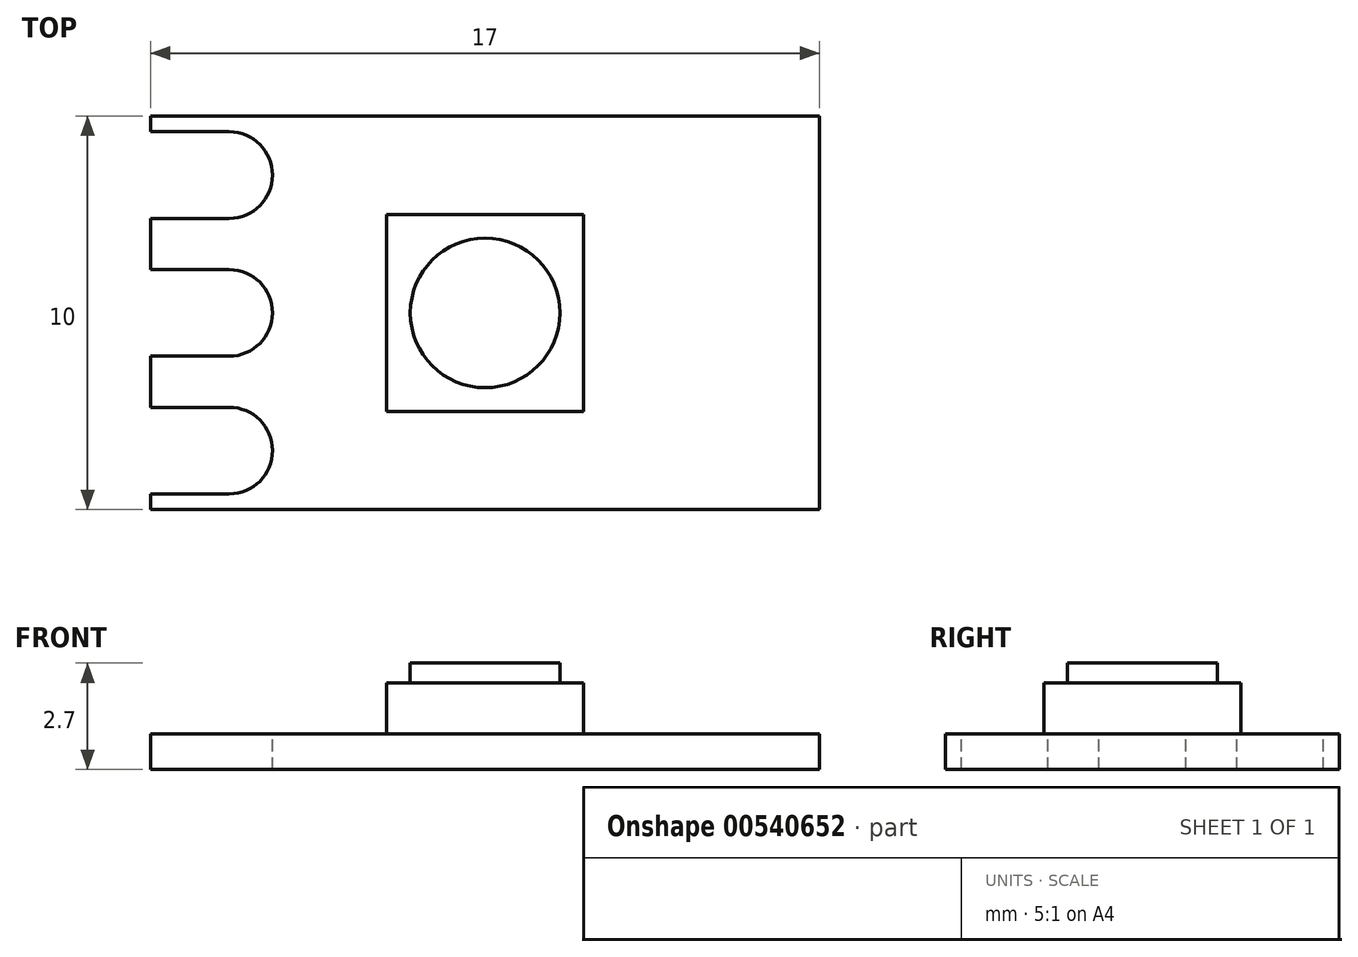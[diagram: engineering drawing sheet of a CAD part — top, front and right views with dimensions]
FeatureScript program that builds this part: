
annotation { "Feature Type Name" : "Feature", "Feature Type Description" : "" }
export const myFeature = defineFeature(function(context is Context, id is Id, definition is map)
    precondition{}
    {
        {
            var Q0;
            Q0=qCreatedBy(makeId("Top.planeOp"),FACE);
            var sketch = newSketch(context, id + "F0", { "sketchPlane" : qUnion([Q0])});
            skLineSegment(sketch, "E0.bottom", {"start": v(8.5, -5) * mm, "end": v(-8.5, -5) * mm});
            skLineSegment(sketch, "E0.top", {"start": v(8.5, 5) * mm, "end": v(-8.5, 5) * mm});
            skLineSegment(sketch, "E0.left", {"start": v(136, -5) * mm, "end": v(136, 5) * mm});
            skLineSegment(sketch, "E0.right", {"start": v(-8.5, -5) * mm, "end": v(-8.5, 5) * mm});
            skPoint(sketch, "E0.middle", {"position": v(0, 0) * mm});
            skLineSegment(sketch, "E1", {"start": v(8.5, 5) * mm, "end": v(8.5, -5) * mm});
            skLineSegment(sketch, "E2", {"start": v(-8.5, 0) * mm, "end": v(8.5, 0) * mm, "construction": true});
            skLineSegment(sketch, "E3.bottom", {"start": v(2.5, -2.5) * mm, "end": v(-2.5, -2.5) * mm});
            skLineSegment(sketch, "E3.top", {"start": v(2.5, 2.5) * mm, "end": v(-2.5, 2.5) * mm});
            skLineSegment(sketch, "E3.left", {"start": v(2.5, -2.5) * mm, "end": v(2.5, 2.5) * mm});
            skLineSegment(sketch, "E3.right", {"start": v(-2.5, -2.5) * mm, "end": v(-2.5, 2.5) * mm});
            skLineSegment(sketch, "E4", {"start": v(-8.5, 3.5) * mm, "end": v(-6.5, 3.5) * mm, "construction": true});
            skArc(sketch, "E5.0.endCap", {"start": v(-6.5, 4.6) * mm, "mid": v(-5.4, 3.5) * mm, "end": v(-6.5, 2.4) * mm});
            skLineSegment(sketch, "E5.0.left", {"start": v(-8.5, 4.6) * mm, "end": v(-6.5, 4.6) * mm});
            skLineSegment(sketch, "E5.0.right", {"start": v(-8.5, 2.4) * mm, "end": v(-6.5, 2.4) * mm});
            skLineSegment(sketch, "E6.0.1.0", {"start": v(-8.5, 0) * mm, "end": v(-6.5, 0) * mm, "construction": true});
            skArc(sketch, "E6.0.1.1", {"start": v(-6.5, 1.1) * mm, "mid": v(-5.4, 0) * mm, "end": v(-6.5, -1.1) * mm});
            skLineSegment(sketch, "E6.0.1.2", {"start": v(-8.5, 1.1) * mm, "end": v(-6.5, 1.1) * mm});
            skLineSegment(sketch, "E6.0.1.4", {"start": v(-8.5, -1.1) * mm, "end": v(-6.5, -1.1) * mm});
            skLineSegment(sketch, "E6.0.2.0", {"start": v(-8.5, -3.5) * mm, "end": v(-6.5, -3.5) * mm, "construction": true});
            skArc(sketch, "E6.0.2.1", {"start": v(-6.5, -2.4) * mm, "mid": v(-5.4, -3.5) * mm, "end": v(-6.5, -4.6) * mm});
            skLineSegment(sketch, "E6.0.2.2", {"start": v(-8.5, -2.4) * mm, "end": v(-6.5, -2.4) * mm});
            skLineSegment(sketch, "E6.0.2.4", {"start": v(-8.5, -4.6) * mm, "end": v(-6.5, -4.6) * mm});
            skLineSegment(sketch, "E6.1.0.0", {"start": v(6.5, 3.5) * mm, "end": v(8.5, 3.5) * mm, "construction": true});
            skLineSegment(sketch, "E6.1.0.2", {"start": v(6.5, 4.6) * mm, "end": v(8.5, 4.6) * mm});
            skArc(sketch, "E6.1.0.3", {"start": v(6.5, 2.4) * mm, "mid": v(5.4, 3.5) * mm, "end": v(6.5, 4.6) * mm});
            skLineSegment(sketch, "E6.1.0.4", {"start": v(6.5, 2.4) * mm, "end": v(8.5, 2.4) * mm});
            skLineSegment(sketch, "E6.1.1.0", {"start": v(6.5, 0) * mm, "end": v(8.5, 0) * mm, "construction": true});
            skLineSegment(sketch, "E6.1.1.2", {"start": v(6.5, 1.1) * mm, "end": v(8.5, 1.1) * mm});
            skArc(sketch, "E6.1.1.3", {"start": v(6.5, -1.1) * mm, "mid": v(5.4, 0) * mm, "end": v(6.5, 1.1) * mm});
            skLineSegment(sketch, "E6.1.1.4", {"start": v(6.5, -1.1) * mm, "end": v(8.5, -1.1) * mm});
            skLineSegment(sketch, "E6.1.2.0", {"start": v(6.5, -3.5) * mm, "end": v(8.5, -3.5) * mm, "construction": true});
            skLineSegment(sketch, "E6.1.2.2", {"start": v(6.5, -2.4) * mm, "end": v(8.5, -2.4) * mm});
            skArc(sketch, "E6.1.2.3", {"start": v(6.5, -4.6) * mm, "mid": v(5.4, -3.5) * mm, "end": v(6.5, -2.4) * mm});
            skLineSegment(sketch, "E6.1.2.4", {"start": v(6.5, -4.6) * mm, "end": v(8.5, -4.6) * mm});
            skLineSegment(sketch, "E6.direction1", {"start": v(-8.5, 2.4) * mm, "end": v(6.5, 2.4) * mm, "construction": true});
            skLineSegment(sketch, "E6.direction2", {"start": v(-10.5, 2.4) * mm, "end": v(-10.5, -1.1) * mm, "construction": true});
            skPoint(sketch, "E7", {"position": v(-8.5, 3.5) * mm});
            skPoint(sketch, "E8", {"position": v(8.5, 3.5) * mm});
            skPoint(sketch, "E9", {"position": v(-8.5, 0) * mm});
            skPoint(sketch, "E10", {"position": v(8.5, 0) * mm});
            skPoint(sketch, "E11.orphan", {"position": v(10.5, -2.4) * mm});
            skPoint(sketch, "E12.orphan", {"position": v(10.5, -3.5) * mm});
            skPoint(sketch, "E13.orphan", {"position": v(10.5, 1.1) * mm});
            skPoint(sketch, "E14.orphan", {"position": v(10.5, 0) * mm});
            skPoint(sketch, "E15.orphan", {"position": v(10.5, 4.6) * mm});
            skPoint(sketch, "E16.orphan", {"position": v(10.5, 3.5) * mm});
            skPoint(sketch, "E17.orphan", {"position": v(-10.5, -2.4) * mm});
            skPoint(sketch, "E18.orphan", {"position": v(-10.5, 1.1) * mm});
            skPoint(sketch, "E19.orphan", {"position": v(-10.5, 0) * mm});
            skPoint(sketch, "E20.orphan", {"position": v(-10.5, 4.6) * mm});
            skPoint(sketch, "E21.orphan", {"position": v(-10.5, 3.5) * mm});
            skPoint(sketch, "E22.orphan", {"position": v(-10.5, -3.5) * mm});
            skSolve(sketch);
        }
        {
            var Q0;
            {var subQ6=sQuery(id+"F0.wireOp",EDGE,"E0.bottom");Q0=makeQuery(id+"F0.imprint","IMPRINT",FACE,{"disambiguationData":[TD([[makeQuery(id+"F0.imprint","IMPRINT",EDGE,{"derivedFrom":subQ6}),-1.0]])]});}
            var Q1;
            Q1=makeQuery(id+"F0.imprint","IMPRINT",FACE,{"disambiguationData":[TD([[makeQuery(id+"F0.imprint","IMPRINT",EDGE,{"derivedFrom":sQuery(id+"F0.wireOp",EDGE,"E5.0.endCap")}),-1.0]])]});
            var Q2;
            Q2=makeQuery(id+"F0.imprint","IMPRINT",FACE,{"disambiguationData":[TD([[makeQuery(id+"F0.imprint","IMPRINT",EDGE,{"derivedFrom":sQuery(id+"F0.wireOp",EDGE,"E6.0.1.1")}),-1.0]])]});
            var Q3;
            Q3=makeQuery(id+"F0.imprint","IMPRINT",FACE,{"disambiguationData":[TD([[makeQuery(id+"F0.imprint","IMPRINT",EDGE,{"derivedFrom":sQuery(id+"F0.wireOp",EDGE,"E6.0.2.1")}),-1.0]])]});
            var Q4;
            {var subQ0=sQuery(id+"F0.wireOp",EDGE,"E6.1.2.2");Q4=makeQuery(id+"F0.imprint","IMPRINT",FACE,{"disambiguationData":[TD([[makeQuery(id+"F0.imprint","IMPRINT",EDGE,{"derivedFrom":subQ0}),-1.0]])]});}
            var Q5;
            {var subQ0=sQuery(id+"F0.wireOp",EDGE,"E6.1.1.2");Q5=makeQuery(id+"F0.imprint","IMPRINT",FACE,{"disambiguationData":[TD([[makeQuery(id+"F0.imprint","IMPRINT",EDGE,{"derivedFrom":subQ0}),-1.0]])]});}
            var Q6;
            {var subQ0=sQuery(id+"F0.wireOp",EDGE,"E6.1.0.2");Q6=makeQuery(id+"F0.imprint","IMPRINT",FACE,{"disambiguationData":[TD([[makeQuery(id+"F0.imprint","IMPRINT",EDGE,{"derivedFrom":subQ0}),-1.0]])]});}
            var Q7;
            Q7=makeQuery(id+"F0.imprint","IMPRINT",FACE,{"disambiguationData":[TD([[makeQuery(id+"F0.imprint","IMPRINT",EDGE,{"derivedFrom":sQuery(id+"F0.wireOp",EDGE,"E3.bottom")}),-1.0]])]});
            extrude(context, id + "F1", {"entities" : qUnion([Q0, Q1, Q2, Q3, Q4, Q5, Q6, Q7]), "oppositeDirection" : true, "depth" : .4 * mm, "offsetDistance" : 25 * mm});
        }
        {
            var Q0;
            Q0=makeQuery(id+"F0.imprint","IMPRINT",FACE,{"disambiguationData":[TD([[makeQuery(id+"F0.imprint","IMPRINT",EDGE,{"derivedFrom":sQuery(id+"F0.wireOp",EDGE,"E6.0.2.1")}),-1.0]])]});
            var Q1;
            Q1=makeQuery(id+"F0.imprint","IMPRINT",FACE,{"disambiguationData":[TD([[makeQuery(id+"F0.imprint","IMPRINT",EDGE,{"derivedFrom":sQuery(id+"F0.wireOp",EDGE,"E6.0.1.1")}),-1.0]])]});
            var Q2;
            Q2=makeQuery(id+"F0.imprint","IMPRINT",FACE,{"disambiguationData":[TD([[makeQuery(id+"F0.imprint","IMPRINT",EDGE,{"derivedFrom":sQuery(id+"F0.wireOp",EDGE,"E5.0.endCap")}),-1.0]])]});
            var Q3;
            {var subQ0=sQuery(id+"F0.wireOp",EDGE,"E6.1.0.2");Q3=makeQuery(id+"F0.imprint","IMPRINT",FACE,{"disambiguationData":[TD([[makeQuery(id+"F0.imprint","IMPRINT",EDGE,{"derivedFrom":subQ0}),-1.0]])]});}
            var Q4;
            {var subQ0=sQuery(id+"F0.wireOp",EDGE,"E6.1.1.2");Q4=makeQuery(id+"F0.imprint","IMPRINT",FACE,{"disambiguationData":[TD([[makeQuery(id+"F0.imprint","IMPRINT",EDGE,{"derivedFrom":subQ0}),-1.0]])]});}
            var Q5;
            {var subQ0=sQuery(id+"F0.wireOp",EDGE,"E6.1.2.2");Q5=makeQuery(id+"F0.imprint","IMPRINT",FACE,{"disambiguationData":[TD([[makeQuery(id+"F0.imprint","IMPRINT",EDGE,{"derivedFrom":subQ0}),-1.0]])]});}
            extrude(context, id + "F2", {"entities" : qUnion([Q0, Q1, Q2, Q3, Q4, Q5]), "operationType" : NewBodyOperationType.ADD, "depth" : .5 * mm, "offsetDistance" : 25 * mm});
        }
        {
            var Q0;
            Q0=makeQuery(id+"F0.imprint","IMPRINT",FACE,{"disambiguationData":[TD([[makeQuery(id+"F0.imprint","IMPRINT",EDGE,{"derivedFrom":sQuery(id+"F0.wireOp",EDGE,"E3.bottom")}),-1.0]])]});
            extrude(context, id + "F3", {"entities" : qUnion([Q0]), "operationType" : NewBodyOperationType.ADD, "depth" : 1.8 * mm, "offsetDistance" : 25 * mm});
        }
        {
            var Q0;
            Q0=makeQuery(id+"F3.opExtrude","CAP_FACE",FACE,{"disambiguationData":[OSD([sQuery(id+"F0.wireOp",EDGE,"E3.bottom"),sQuery(id+"F0.wireOp",EDGE,"E3.top"),sQuery(id+"F0.wireOp",EDGE,"E3.left"),sQuery(id+"F0.wireOp",EDGE,"E3.right")])],"isStart":false});
            var sketch = newSketch(context, id + "F4", { "sketchPlane" : qUnion([Q0])});
            skCircle(sketch, "E23", {"center": v(0, 0) * mm, "radius": 1.9 * mm});
            skPoint(sketch, "E23.centerSnap0", {"position": v(2.5, 0) * mm});
            skPoint(sketch, "E23.centerSnap1", {"position": v(0, 2.5) * mm});
            skSolve(sketch);
        }
        {
            var Q0;
            Q0=makeQuery(id+"F4.imprint","IMPRINT",FACE,{"disambiguationData":[TD([[makeQuery(id+"F4.imprint","IMPRINT",EDGE,{"derivedFrom":sQuery(id+"F4.wireOp",EDGE,"E23")}),1.0]])]});
            extrude(context, id + "F5", {"entities" : qUnion([Q0]), "operationType" : NewBodyOperationType.ADD, "depth" : .5 * mm, "offsetDistance" : 25 * mm});
        }
    });
